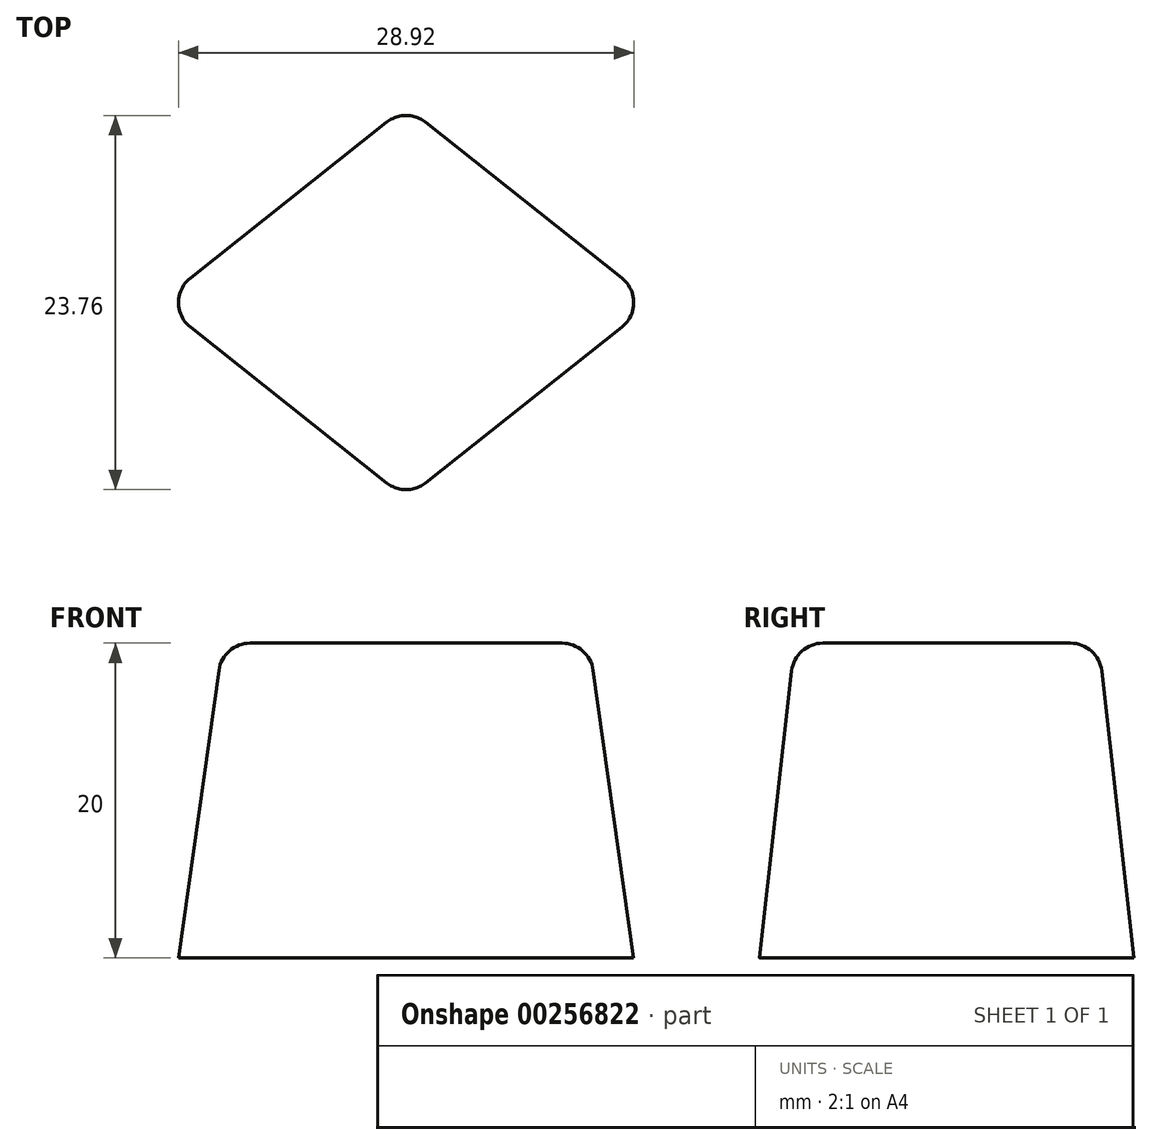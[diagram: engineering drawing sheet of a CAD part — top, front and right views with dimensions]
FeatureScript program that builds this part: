
annotation { "Feature Type Name" : "Feature", "Feature Type Description" : "" }
export const myFeature = defineFeature(function(context is Context, id is Id, definition is map)
    precondition{}
    {
        {
            var Q0;
            Q0=qCreatedBy(makeId("Top.planeOp"),FACE);
            var sketch = newSketch(context, id + "F0", { "sketchPlane" : qUnion([Q0])});
            skLineSegment(sketch, "E0", {"start": v(0, 12.43) * mm, "end": v(15.66, 0) * mm});
            skLineSegment(sketch, "E1", {"start": v(0, 12.43) * mm, "end": v(-15.66, 0) * mm});
            skLineSegment(sketch, "E2.MirrorCS", {"start": v(0, -12.43) * mm, "end": v(-15.66, 0) * mm});
            skLineSegment(sketch, "E3.MirrorCS", {"start": v(0, -12.43) * mm, "end": v(15.66, 0) * mm});
            skSolve(sketch);
        }
        {
            var Q0;
            Q0=qSketchRegion(id+"F0",true);
            extrude(context, id + "F1", {"entities" : qUnion([Q0]), "depth" : 20 * mm, "hasDraft" : true, "draftAngle" : 5 * degree, "draftPullDirection" : true});
        }
        {
            var Q0;
            Q0=makeQuery(id+"F1.opExtrude","CAP_EDGE",EDGE,{"disambiguationData":[OSD([sQuery(id+"F0.wireOp",EDGE,"E3.MirrorCS")])],"isStart":false});
            var Q1;
            Q1=makeQuery(id+"F1.opExtrude","CAP_EDGE",EDGE,{"disambiguationData":[OSD([sQuery(id+"F0.wireOp",EDGE,"E2.MirrorCS")])],"isStart":false});
            var Q2;
            Q2=makeQuery(id+"F1.opExtrude","CAP_EDGE",EDGE,{"disambiguationData":[OSD([sQuery(id+"F0.wireOp",EDGE,"E1")])],"isStart":false});
            var Q3;
            Q3=makeQuery(id+"F1.opExtrude","CAP_EDGE",EDGE,{"disambiguationData":[OSD([sQuery(id+"F0.wireOp",EDGE,"E0")])],"isStart":false});
            var Q4;
            Q4=makeQuery(id+"F1.opExtrude","SWEPT_EDGE",EDGE,{"disambiguationData":[OSD([sQuery(id+"F0.wireOp",EDGE,"E1"),sQuery(id+"F0.wireOp",EDGE,"E2.MirrorCS")])]});
            var Q5;
            Q5=makeQuery(id+"F1.opExtrude","SWEPT_EDGE",EDGE,{"disambiguationData":[OSD([sQuery(id+"F0.wireOp",EDGE,"E0"),sQuery(id+"F0.wireOp",EDGE,"E1")])]});
            var Q6;
            Q6=makeQuery(id+"F1.opExtrude","SWEPT_EDGE",EDGE,{"disambiguationData":[OSD([sQuery(id+"F0.wireOp",EDGE,"E0"),sQuery(id+"F0.wireOp",EDGE,"E3.MirrorCS")])]});
            var Q7;
            Q7=makeQuery(id+"F1.opExtrude","SWEPT_EDGE",EDGE,{"disambiguationData":[OSD([sQuery(id+"F0.wireOp",EDGE,"E2.MirrorCS"),sQuery(id+"F0.wireOp",EDGE,"E3.MirrorCS")])]});
            fillet(context, id + "F2", {"entities" : qUnion([Q0, Q1, Q2, Q3, Q4, Q5, Q6, Q7]), "radius" : 2 * mm, "tangentPropagation" : true, "allowEdgeOverflow" : false});
        }
    });
